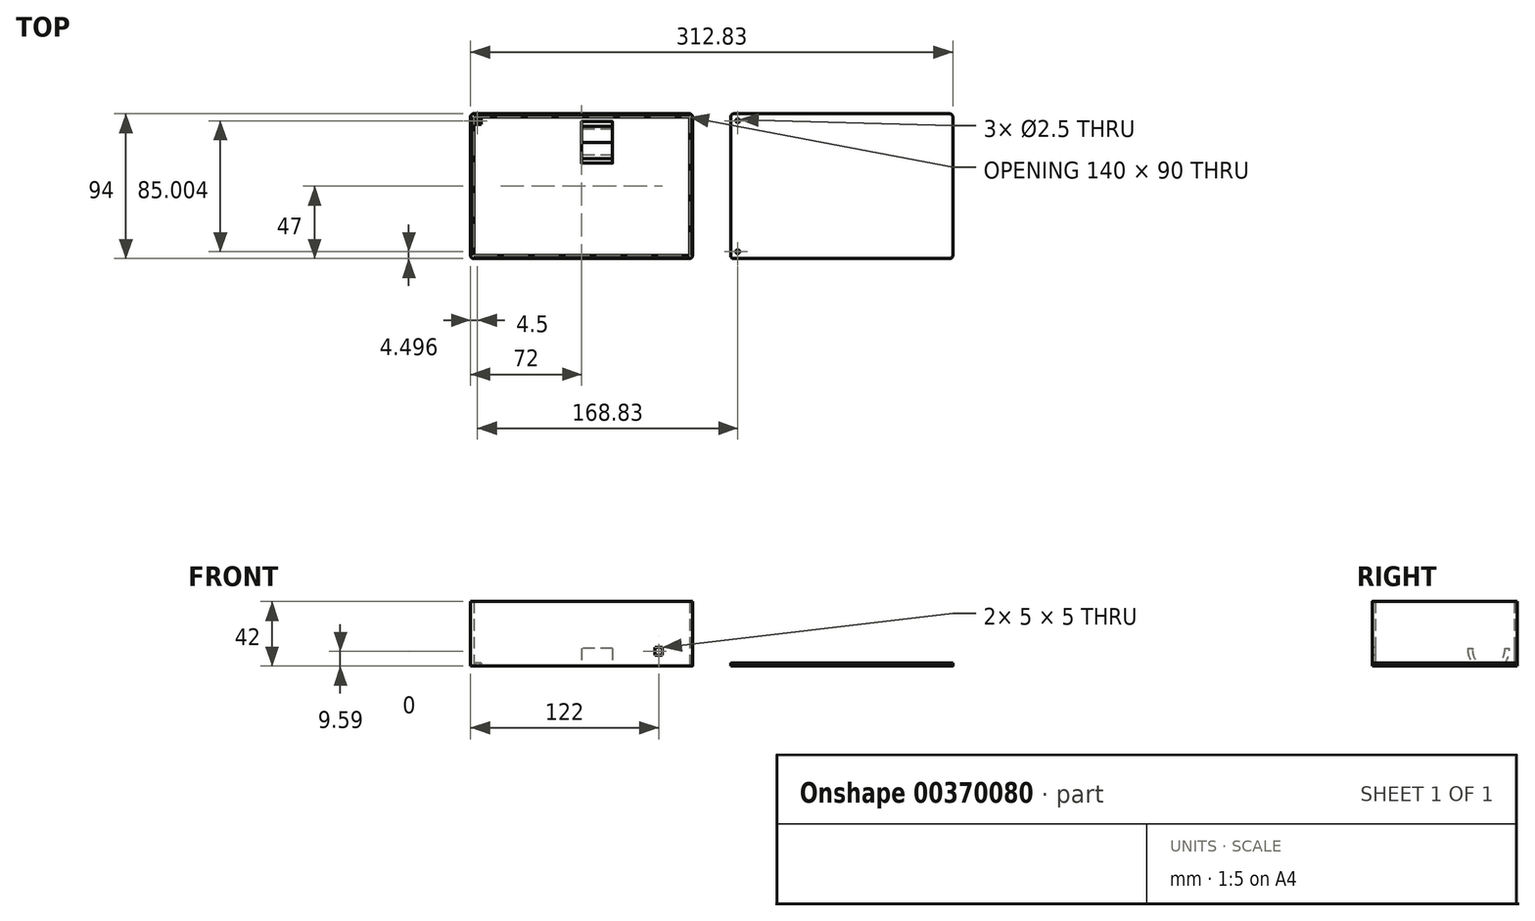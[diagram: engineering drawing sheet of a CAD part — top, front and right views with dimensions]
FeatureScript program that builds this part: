
annotation { "Feature Type Name" : "Feature", "Feature Type Description" : "" }
export const myFeature = defineFeature(function(context is Context, id is Id, definition is map)
    precondition{}
    {
        {
            var Q0;
            Q0=qCreatedBy(makeId("Top.planeOp"),FACE);
            var sketch = newSketch(context, id + "F0", { "sketchPlane" : qUnion([Q0])});
            skLineSegment(sketch, "E0.bottom", {"start": v(70, 45) * mm, "end": v(-70, 45) * mm});
            skLineSegment(sketch, "E0.top", {"start": v(70, -45) * mm, "end": v(-70, -45) * mm});
            skLineSegment(sketch, "E0.left", {"start": v(70, 45) * mm, "end": v(70, -45) * mm});
            skLineSegment(sketch, "E0.right", {"start": v(-70, 45) * mm, "end": v(-70, -45) * mm});
            skPoint(sketch, "E0.middle", {"position": v(0, 0) * mm});
            skPoint(sketch, "E1", {"position": v(-6.5, -40) * mm});
            skPoint(sketch, "E2", {"position": v(65, -35) * mm});
            skPoint(sketch, "E3", {"position": v(65, -6.5) * mm});
            skPoint(sketch, "E4", {"position": v(-6.5, 9) * mm});
            skCircle(sketch, "E5", {"center": v(-6.5, 9) * mm, "radius": 1.25 * mm});
            skCircle(sketch, "E6", {"center": v(65, -6.5) * mm, "radius": 1.25 * mm});
            skCircle(sketch, "E7", {"center": v(65, -35) * mm, "radius": 1.25 * mm});
            skCircle(sketch, "E8", {"center": v(-6.5, -40) * mm, "radius": 1.25 * mm});
            skLineSegment(sketch, "E9.bottom", {"start": v(70, 47) * mm, "end": v(-70, 47) * mm});
            skLineSegment(sketch, "E9.top", {"start": v(70, -47) * mm, "end": v(-70, -47) * mm});
            skLineSegment(sketch, "E9.left", {"start": v(72, 45) * mm, "end": v(72, -45) * mm});
            skLineSegment(sketch, "E9.right", {"start": v(-72, 45) * mm, "end": v(-72, -45) * mm});
            skPoint(sketch, "E10.visualSharp", {"position": v(-72, 47) * mm});
            skArc(sketch, "E10.filletArc", {"start": v(-70, 47) * mm, "mid": v(-71.41, 46.41) * mm, "end": v(-72, 45) * mm});
            skPoint(sketch, "E11.visualSharp", {"position": v(72, 47) * mm});
            skArc(sketch, "E11.filletArc", {"start": v(72, 45) * mm, "mid": v(71.41, 46.41) * mm, "end": v(70, 47) * mm});
            skPoint(sketch, "E12.visualSharp", {"position": v(72, -47) * mm});
            skArc(sketch, "E12.filletArc", {"start": v(70, -47) * mm, "mid": v(71.41, -46.41) * mm, "end": v(72, -45) * mm});
            skPoint(sketch, "E13.visualSharp", {"position": v(-72, -47) * mm});
            skArc(sketch, "E13.filletArc", {"start": v(-72, -45) * mm, "mid": v(-71.41, -46.41) * mm, "end": v(-70, -47) * mm});
            skLineSegment(sketch, "E14.bottom", {"start": v(-70, 45) * mm, "end": v(-65, 45) * mm});
            skLineSegment(sketch, "E14.top", {"start": v(-70, 40) * mm, "end": v(-65, 40) * mm});
            skLineSegment(sketch, "E14.left", {"start": v(-70, 45) * mm, "end": v(-70, 40) * mm});
            skLineSegment(sketch, "E14.right", {"start": v(-65, 45) * mm, "end": v(-65, 40) * mm});
            skPoint(sketch, "E15", {"position": v(-67.5, 42.5) * mm});
            skLineSegment(sketch, "E16.bottom", {"start": v(-65, -45) * mm, "end": v(-70, -45) * mm});
            skLineSegment(sketch, "E16.top", {"start": v(-65, -40) * mm, "end": v(-70, -40) * mm});
            skLineSegment(sketch, "E16.left", {"start": v(-65, -45) * mm, "end": v(-65, -40) * mm});
            skLineSegment(sketch, "E16.right", {"start": v(-70, -45) * mm, "end": v(-70, -40) * mm});
            skPoint(sketch, "E17", {"position": v(-67.5, -42.5) * mm});
            skSolve(sketch);
        }
        {
            var Q0;
            Q0=makeQuery(id+"F0.imprint","IMPRINT",FACE,{"disambiguationData":[TD([[makeQuery(id+"F0.imprint","IMPRINT",EDGE,{"derivedFrom":sQuery(id+"F0.wireOp",EDGE,"E0.bottom")}),1.0]])]});
            extrude(context, id + "F1", {"entities" : qUnion([Q0]), "depth" : 2 * mm});
        }
        {
            var Q0;
            Q0=makeQuery(id+"F0.imprint","IMPRINT",FACE,{"disambiguationData":[TD([[makeQuery(id+"F0.imprint","IMPRINT",EDGE,{"derivedFrom":sQuery(id+"F0.wireOp",EDGE,"E0.bottom")}),-1.0]])]});
            var Q1;
            Q1=makeQuery(id+"F0.imprint","IMPRINT",FACE,{"disambiguationData":[TD([[makeQuery(id+"F0.imprint","IMPRINT",EDGE,{"derivedFrom":sQuery(id+"F0.wireOp",EDGE,"E14.bottom")}),-1.0]])]});
            var Q2;
            Q2=makeQuery(id+"F0.imprint","IMPRINT",FACE,{"disambiguationData":[TD([[makeQuery(id+"F0.imprint","IMPRINT",EDGE,{"derivedFrom":sQuery(id+"F0.wireOp",EDGE,"E16.bottom")}),-1.0]])]});
            extrude(context, id + "F2", {"entities" : qUnion([Q0, Q1, Q2]), "operationType" : NewBodyOperationType.ADD, "depth" : 42 * mm});
        }
        {
            var Q0;
            Q0=qCreatedBy(makeId("Right.planeOp"),FACE);
            var sketch = newSketch(context, id + "F3", { "sketchPlane" : qUnion([Q0])});
            skPoint(sketch, "E18", {"position": v(43, 0) * mm});
            skLineSegment(sketch, "E19", {"start": v(20.01, 0) * mm, "end": v(28.5, 0) * mm});
            skLineSegment(sketch, "E20", {"start": v(18.04, 11.46) * mm, "end": v(18.04, 11.46) * mm});
            skPoint(sketch, "E21", {"position": v(28.47, 0) * mm});
            skLineSegment(sketch, "E22", {"start": v(19.98, 0) * mm, "end": v(36.96, 0) * mm});
            skArc(sketch, "E23", {"start": v(36.96, 0) * mm, "mid": v(40.85, 5.12) * mm, "end": v(41.94, 11.46) * mm});
            skArc(sketch, "E24", {"start": v(18, 11.46) * mm, "mid": v(28.47, 0) * mm, "end": v(38.93, 11.46) * mm});
            skArc(sketch, "E25", {"start": v(15, 11.46) * mm, "mid": v(16.09, 5.12) * mm, "end": v(19.98, 0) * mm});
            skLineSegment(sketch, "E26", {"start": v(15, 11.46) * mm, "end": v(18, 11.46) * mm});
            skLineSegment(sketch, "E27", {"start": v(38.93, 11.46) * mm, "end": v(41.94, 11.46) * mm});
            skLineSegment(sketch, "E28", {"start": v(28.5, 0) * mm, "end": v(36.99, 0) * mm});
            skSolve(sketch);
        }
        {
            var Q0;
            {var subQ0=sQuery(id+"F3.wireOp",EDGE,"E25");Q0=makeQuery(id+"F3.imprint","IMPRINT",FACE,{"disambiguationData":[TD([[makeQuery(id+"F3.imprint","IMPRINT",EDGE,{"derivedFrom":subQ0}),1.0]])]});}
            var Q1;
            {var subQ4=sQuery(id+"F3.wireOp",EDGE,"E23");Q1=makeQuery(id+"F3.imprint","IMPRINT",FACE,{"disambiguationData":[TD([[makeQuery(id+"F3.imprint","IMPRINT",EDGE,{"derivedFrom":subQ4}),1.0]])]});}
            extrude(context, id + "F4", {"entities" : qUnion([Q0, Q1]), "operationType" : NewBodyOperationType.ADD, "depth" : 20 * mm});
        }
        {
            var Q0;
            Q0=makeQuery(id+"F2.opExtrude","CAP_FACE",FACE,{"disambiguationData":[OSD([sQuery(id+"F0.wireOp",EDGE,"E0.bottom"),sQuery(id+"F0.wireOp",EDGE,"E0.top"),sQuery(id+"F0.wireOp",EDGE,"E0.left"),sQuery(id+"F0.wireOp",EDGE,"E0.right"),sQuery(id+"F0.wireOp",EDGE,"E9.bottom"),sQuery(id+"F0.wireOp",EDGE,"E9.top"),sQuery(id+"F0.wireOp",EDGE,"E9.left"),sQuery(id+"F0.wireOp",EDGE,"E9.right"),sQuery(id+"F0.wireOp",EDGE,"E10.filletArc"),sQuery(id+"F0.wireOp",EDGE,"E11.filletArc"),sQuery(id+"F0.wireOp",EDGE,"E12.filletArc"),sQuery(id+"F0.wireOp",EDGE,"E13.filletArc")])],"isStart":false});
            var sketch = newSketch(context, id + "F5", { "sketchPlane" : qUnion([Q0])});
            skPoint(sketch, "E29.middle", {"position": v(168.83, 0) * mm});
            skLineSegment(sketch, "E30.bottom", {"start": v(238.83, 47) * mm, "end": v(98.83, 47) * mm});
            skLineSegment(sketch, "E30.top", {"start": v(238.83, -47) * mm, "end": v(98.83, -47) * mm});
            skLineSegment(sketch, "E30.left", {"start": v(240.83, 45) * mm, "end": v(240.83, -45) * mm});
            skLineSegment(sketch, "E30.right", {"start": v(96.83, 45) * mm, "end": v(96.83, -45) * mm});
            skPoint(sketch, "E31.visualSharp", {"position": v(96.83, 47) * mm});
            skArc(sketch, "E31.filletArc", {"start": v(98.83, 47) * mm, "mid": v(97.42, 46.41) * mm, "end": v(96.83, 45) * mm});
            skPoint(sketch, "E32.visualSharp", {"position": v(240.83, 47) * mm});
            skArc(sketch, "E32.filletArc", {"start": v(240.83, 45) * mm, "mid": v(240.24, 46.41) * mm, "end": v(238.83, 47) * mm});
            skPoint(sketch, "E33.visualSharp", {"position": v(240.83, -47) * mm});
            skArc(sketch, "E33.filletArc", {"start": v(238.83, -47) * mm, "mid": v(240.24, -46.41) * mm, "end": v(240.83, -45) * mm});
            skPoint(sketch, "E34.visualSharp", {"position": v(96.83, -47) * mm});
            skArc(sketch, "E34.filletArc", {"start": v(96.83, -45) * mm, "mid": v(97.42, -46.41) * mm, "end": v(98.83, -47) * mm});
            skCircle(sketch, "E35", {"center": v(101.33, 42.5) * mm, "radius": 1.25 * mm});
            skPoint(sketch, "E36", {"position": v(101.33, -42.5) * mm});
            skCircle(sketch, "E37", {"center": v(101.33, -42.5) * mm, "radius": 1.25 * mm});
            skSolve(sketch);
        }
        {
            var Q0;
            Q0=sQuery(id+"F0.wireOp",VERTEX,"E15");
            var Q1;
            Q1=sQuery(id+"F0.wireOp",VERTEX,"E17");
            var Q2;
            Q2=makeQuery(id+"F1.opExtrude","SWEPT_BODY",BODY,{"disambiguationData":[OSD([sQuery(id+"F0.wireOp",EDGE,"E0.bottom"),sQuery(id+"F0.wireOp",EDGE,"E0.top"),sQuery(id+"F0.wireOp",EDGE,"E0.left"),sQuery(id+"F0.wireOp",EDGE,"E0.right"),sQuery(id+"F0.wireOp",EDGE,"E5"),sQuery(id+"F0.wireOp",EDGE,"E6"),sQuery(id+"F0.wireOp",EDGE,"E7"),sQuery(id+"F0.wireOp",EDGE,"E8"),sQuery(id+"F0.wireOp",EDGE,"E14.top"),sQuery(id+"F0.wireOp",EDGE,"E14.right")])]});
            hole(context, id + "F6", {"style" : HoleStyle.SIMPLE, "endStyle" : HoleEndStyle.BLIND, "oppositeDirection" : true, "holeDiameter" : 2.5 * mm, "holeDepth" : 100 * mm, "isTappedThrough" : true, "tappedDepth" : 12.7 * mm, "tapClearance" : 3, "locations" : qUnion([Q0, Q1]), "scope" : qUnion([Q2])});
        }
        {
            var Q0;
            Q0=makeQuery(id+"F5.imprint","IMPRINT",FACE,{"disambiguationData":[TD([[makeQuery(id+"F5.imprint","IMPRINT",EDGE,{"derivedFrom":sQuery(id+"F5.wireOp",EDGE,"E30.bottom")}),1.0]])]});
            extrude(context, id + "F7", {"entities" : qUnion([Q0]), "depth" : 2 * mm});
        }
        {
            var Q0;
            Q0=makeQuery(id+"F7.opExtrude","SWEPT_BODY",BODY,{"disambiguationData":[OSD([sQuery(id+"F5.wireOp",EDGE,"E30.bottom"),sQuery(id+"F5.wireOp",EDGE,"E30.top"),sQuery(id+"F5.wireOp",EDGE,"E30.left"),sQuery(id+"F5.wireOp",EDGE,"E30.right"),sQuery(id+"F5.wireOp",EDGE,"E31.filletArc"),sQuery(id+"F5.wireOp",EDGE,"E32.filletArc"),sQuery(id+"F5.wireOp",EDGE,"E33.filletArc"),sQuery(id+"F5.wireOp",EDGE,"E34.filletArc"),sQuery(id+"F5.wireOp",EDGE,"E35")])]});
            var Q1;
            Q1=qCreatedBy(makeId("Top.planeOp"),FACE);
            transform(context, id + "F8", {"entities" : qUnion([Q0]), "transformType" : TransformType.TRANSLATION_DISTANCE, "transformDirection" : qUnion([Q1]), "distance" : 42 * mm, "oppositeDirection" : true, "makeCopy" : false});
        }
        {
            var Q0;
            Q0=makeQuery(id+"F2.opExtrude","SWEPT_FACE",FACE,{"disambiguationData":[OSD([sQuery(id+"F0.wireOp",EDGE,"E9.top")])]});
            var sketch = newSketch(context, id + "F9", { "sketchPlane" : qUnion([Q0])});
            skPoint(sketch, "E38", {"position": v(50, 9.59) * mm});
            skLineSegment(sketch, "E39.bottom", {"start": v(52.5, 12.09) * mm, "end": v(47.5, 12.09) * mm});
            skLineSegment(sketch, "E39.top", {"start": v(52.5, 7.09) * mm, "end": v(47.5, 7.09) * mm});
            skLineSegment(sketch, "E39.left", {"start": v(52.5, 12.09) * mm, "end": v(52.5, 7.09) * mm});
            skLineSegment(sketch, "E39.right", {"start": v(47.5, 12.09) * mm, "end": v(47.5, 7.09) * mm});
            skSolve(sketch);
        }
        {
            var Q0;
            Q0=makeQuery(id+"F9.imprint","IMPRINT",FACE,{"disambiguationData":[TD([[makeQuery(id+"F9.imprint","IMPRINT",EDGE,{"derivedFrom":sQuery(id+"F9.wireOp",EDGE,"E39.bottom")}),1.0]])]});
            extrude(context, id + "F10", {"entities" : qUnion([Q0]), "operationType" : NewBodyOperationType.REMOVE, "oppositeDirection" : true, "depth" : 254 * mm});
        }
    });
